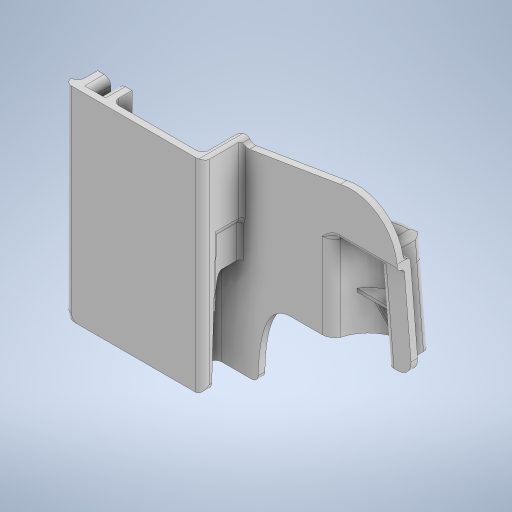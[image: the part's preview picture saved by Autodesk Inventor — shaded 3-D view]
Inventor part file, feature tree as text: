
AUTODESK INVENTOR PART (.ipt)
format: ipt  version: 2023 (Build 270158000, 158)  size: 857,600 bytes
history: native  units: in
note: dims shown in document units (in); Inventor stores cm internally (conversion verified against a paired STEP export)
features: sketch x19, extrude x18, fillet x13, projected_geometry x8, sweep x2, plane x2
ambient origin geometry x8: Origin, YZ Plane, XZ Plane, XY Plane, X Axis, Y Axis, Z Axis, Center Point
bodies: Solid1 (feature_tree)
feature tree (62):
  extrude  "Extrusion1"  Depth=0.1in
  extrude  "Extrusion2"  Depth=0.125in
  extrude  "Extrusion3"  Depth=0.0312in TaperAngle=0.0deg
  sketch  "Sketch4"  dims[d38=0.0625in d39=0.0312in d40=0.0in]
  extrude  "Extrusion8"  Depth=0.5in
  extrude  "Extrusion9"  Depth=0.4375in
  sketch  "Sketch9"  dims[d51=0.375in d52=0.4375in]
  sweep  "Sweep1"
  extrude  "Extrusion12"  TaperAngle=0.0deg  [1 undecoded]
  extrude  "Extrusion14"  Depth=0.05in
  fillet  "Fillet11"  Radius=1.63in
  fillet  "Fillet12"  Radius=0.1in
  fillet  "Fillet13"  Radius=0.1in
  fillet  "Fillet14"  Radius=0.05in
  fillet  "Fillet15"  Radius=0.05in
  extrude  "Extrusion17"  Depth=0.1in TaperAngle=0.0deg
  extrude  "Extrusion18"  Depth=0.1in
  extrude  "Extrusion21"  TaperAngle=0.0deg  [1 undecoded]
  sketch  "Sketch33"  dims[d96=0.1in d103=0.1in d104=0.0in]
  sweep  "Sweep4"
  extrude  "Extrusion22"  Depth=1.5in
  extrude  "Extrusion24"  Depth=0.1in
  extrude  "Extrusion25"  Depth=0.1in
  fillet  "Fillet41"  Radius=0.1in
  fillet  "Fillet42"  Radius=0.7in
  fillet  "Fillet43"  Radius=0.2in
  fillet  "Fillet44"  Radius=0.1in
  fillet  "Fillet46"  Radius=0.05in
  fillet  "Fillet47"  Radius=0.1in
  plane  "Work Plane9"
  extrude  "Extrusion26"  Depth=0.1in
  plane  "Work Plane10"
  extrude  "Extrusion27"  [1 undecoded]
  extrude  "Extrusion28"  Depth=0.1in
  extrude  "Extrusion30"  Depth=0.05in TaperAngle=0.0deg
  extrude  "Extrusion31"  Depth=0.05in TaperAngle=0.0deg
  fillet  "Fillet55"  Radius=2.2in
  fillet  "Fillet57"  Radius=0.1in
  sketch  "Sketch1"  dims[d0=3.0in d1=0.25in d2=2.5in d3=1.75in d5=1.125in d6=2.125in d7=0.1in d8=0.0in]
  sketch  "Sketch2"  dims[d9=0.5in d10=1.0in d11=0.125in d12=0.0625in d13=0.125in d16=0.1in d17=0.0in d20=0.35in]
  sketch  "Sketch3"  dims[d21=0.6in d22=0.0in d23=0.125in d24=1.0in]
  sketch  "Sketch8"  dims[d41=1.0in d42=0.0625in d43=0.375in d44=0.0in d50=0.5in]
  sketch  "3D Sketch1"
  sketch  "Sketch23"  dims[d53=0.1in d55=0.1in]
  sketch  "Sketch27"  dims[d57=0.1in d66=0.0in d67=0.0in]
  sketch  "Sketch28"  dims[d72=1.5in d73=0.0in d87=0.05in d88=1.63in d89=0.0in d92=0.1in d93=0.1in d94=0.05in d95=0.05in]
  projected_geometry  "Projected Loop5"
  projected_geometry  "Projected Loop6"
  sketch  "3D Sketch8"
  sketch  "Sketch36"  dims[d106=0.1in d107=0.0in d114=0.28in]
  projected_geometry  "Projected Loop9"
  sketch  "Sketch37"  dims[d123=0.1in d124=0.0in d125=0.0in d126=0.0in]
  projected_geometry  "Projected Loop11"
  sketch  "Sketch38"  dims[d127=1.4in d128=0.0in d129=0.38in]
  projected_geometry  "Projected Loop12"
  projected_geometry  "Projected Loop13"
  projected_geometry  "Projected Loop14"
  sketch  "Sketch39"  dims[d134=3.2875in d135=0.0in d151=1.5in]
  sketch  "Sketch41"  dims[d156=1.85in d157=0.0in d158=0.1in]
  sketch  "Sketch43"  dims[d160=0.6in d162=0.1in d163=0.1in d164=0.7in d165=0.2in d166=0.1in d167=0.05in d168=0.1in]
  projected_geometry  "Projected Loop15"
  sketch  "Sketch44"  dims[d170=0.2625in d171=0.102in d173=-0.6in d174=0.18in d175=0.05in d176=0.0in d177=0.05in d178=0.0in d180=2.2in d181=0.0in d183=0.1in d184=3.1in d195=0.3in d196=0.0in d197=0.4in d198=0.125in d200=2.9in d201=0.0in d207=0.2in d208=0.06in d209=0.1in d211=0.1in d212=0.525in d18=0.5in d19=0.0344in d33=0.5in d34=0.0344in d35=0.5in d36=0.0344in d37=0.5in d54=0.5in d56=0.5in d58=0.5in d59=0.0344in d68=0.5in d69=0.0344in d70=0.5in d71=0.0344in d76=0.5in d77=0.0344in d78=0.5in d79=0.0344in d80=0.0in d81=0.0in d82=0.5in d83=0.0344in d84=0.5in d85=0.0344in d86=0.0in d90=0.0in d91=0.0344in d97=0.0in d98=0.0in d99=0.0in d105=0.5in d108=0.0in d109=0.0in d110=0.0in d111=0.0in d112=0.0in d113=0.0in d140=0.0in d141=0.0in d142=0.0in d143=0.0in d147=0.0in d148=0.0in d149=0.0in d150=0.0in d154=0.0in d155=0.0in d172=0.0in d193=0.0in d194=0.0in d203=0.0in d204=0.0in d205=0.0in d206=0.0in d210=0.0in d213=0.0in d214=0.0in d215=0.0in d216=0.0in]
note: 3 required parameter values undecoded (feature->parameter linkage not recoverable at this tier; creation-order binding heuristic only, values carry confidence <= 0.55)
